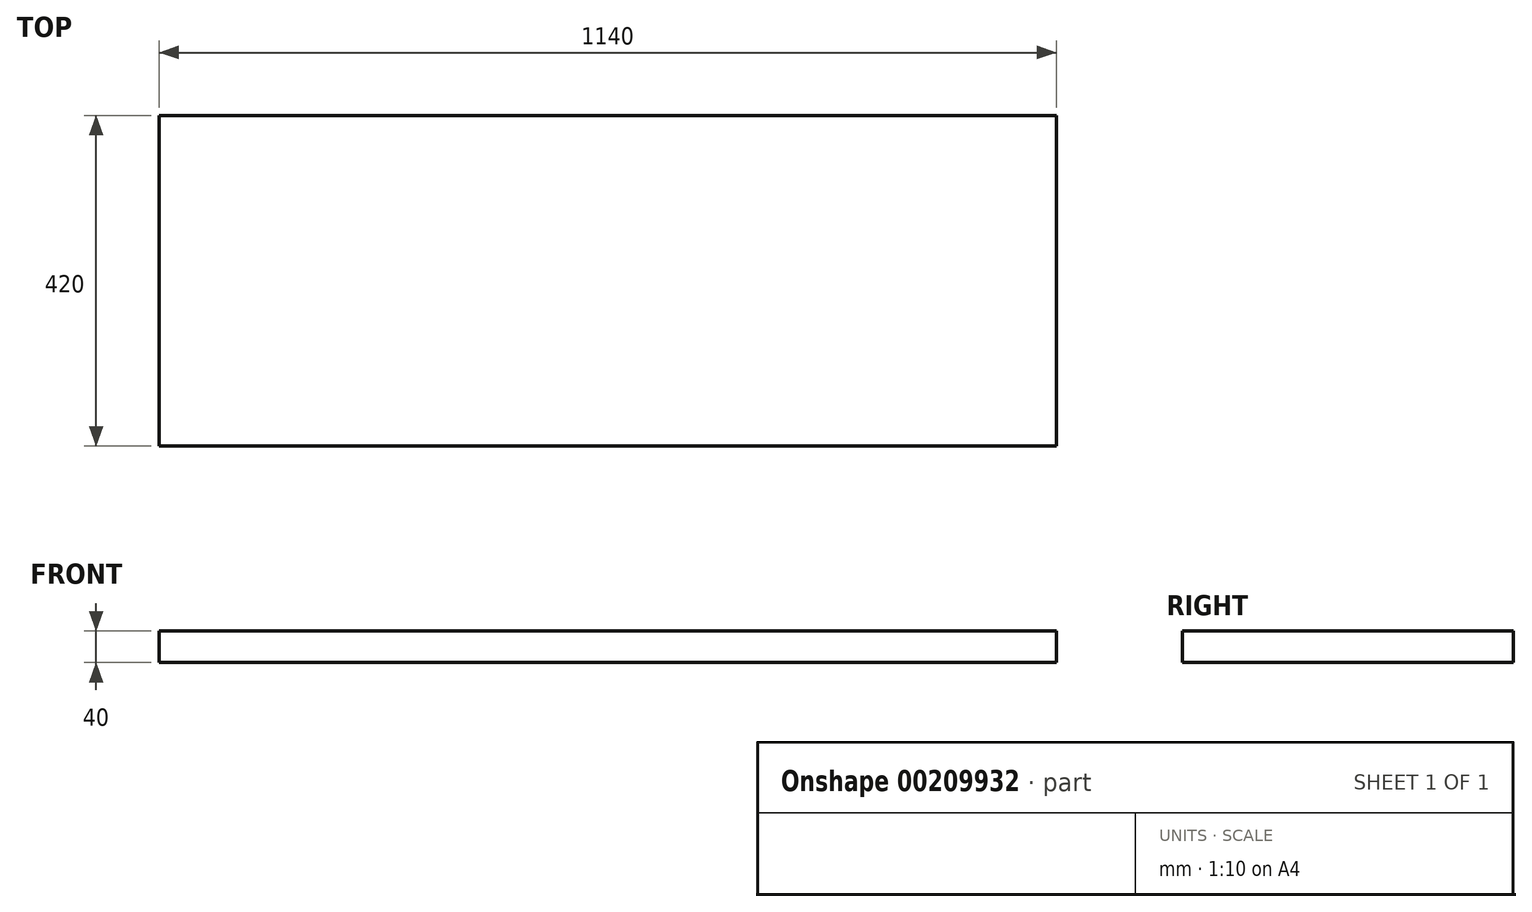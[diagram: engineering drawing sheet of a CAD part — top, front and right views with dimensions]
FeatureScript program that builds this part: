
annotation { "Feature Type Name" : "Feature", "Feature Type Description" : "" }
export const myFeature = defineFeature(function(context is Context, id is Id, definition is map)
    precondition{}
    {
        {
            var Q0;
            Q0=qCreatedBy(makeId("Top.planeOp"),FACE);
            var sketch = newSketch(context, id + "F0", { "sketchPlane" : qUnion([Q0])});
            skLineSegment(sketch, "E0", {"start": v(0, 0) * mm, "end": v(0, -460.76) * mm, "construction": true});
            skLineSegment(sketch, "E1.bottom", {"start": v(-570, 0) * mm, "end": v(390, 0) * mm, "construction": true});
            skLineSegment(sketch, "E1.top", {"start": v(-570, -420) * mm, "end": v(390, -420) * mm, "construction": true});
            skLineSegment(sketch, "E1.left", {"start": v(-570, 0) * mm, "end": v(-570, -420) * mm, "construction": true});
            skLineSegment(sketch, "E1.right", {"start": v(390, 0) * mm, "end": v(390, -420) * mm, "construction": true});
            skLineSegment(sketch, "E2", {"start": v(-390, 0) * mm, "end": v(-390, -610.22) * mm, "construction": true});
            skLineSegment(sketch, "E3", {"start": v(570, 0) * mm, "end": v(570, -629.31) * mm, "construction": true});
            skLineSegment(sketch, "E4.bottom", {"start": v(-570, 0) * mm, "end": v(570, 0) * mm});
            skLineSegment(sketch, "E4.top", {"start": v(-570, -420) * mm, "end": v(570, -420) * mm});
            skLineSegment(sketch, "E4.left", {"start": v(-570, 0) * mm, "end": v(-570, -420) * mm});
            skLineSegment(sketch, "E4.right", {"start": v(570, 0) * mm, "end": v(570, -420) * mm});
            skSolve(sketch);
        }
        {
            var Q0;
            Q0 = qSketchRegion(id + "F0", true);
            extrude(context, id + "F1", {"entities" : qUnion([Q0]), "depth" : 40 * mm});
        }
    });
